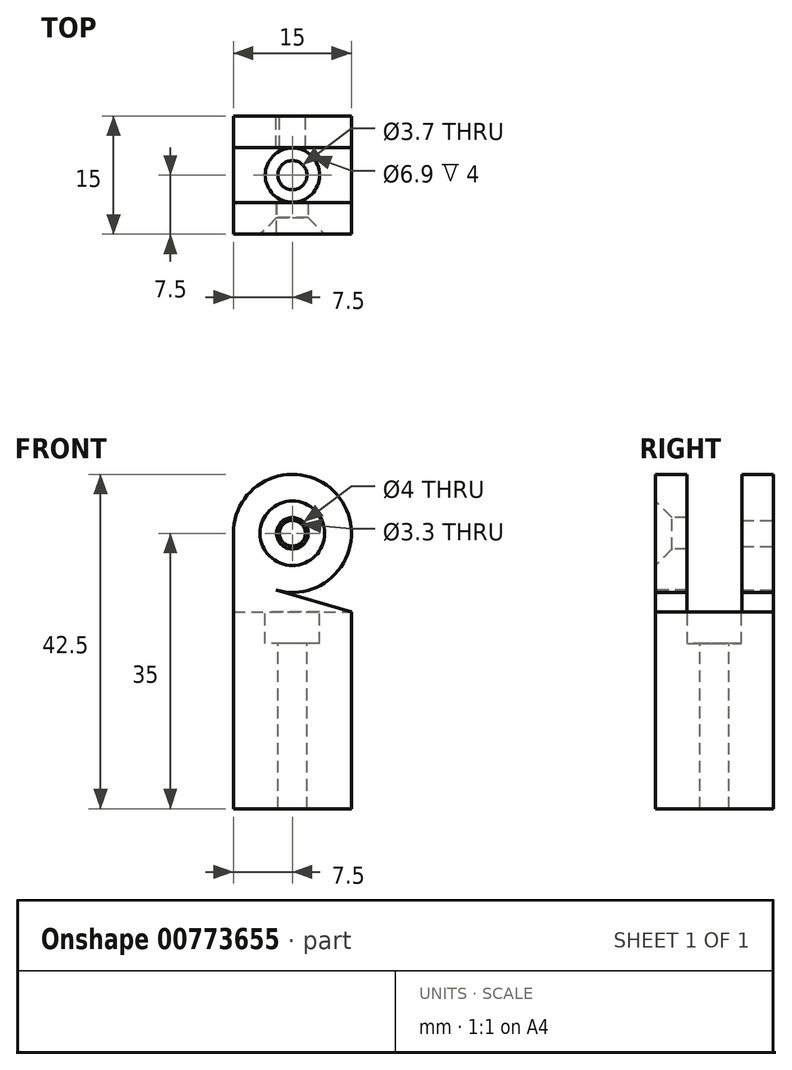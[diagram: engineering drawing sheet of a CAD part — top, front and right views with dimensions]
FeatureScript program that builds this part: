
annotation { "Feature Type Name" : "Feature", "Feature Type Description" : "" }
export const myFeature = defineFeature(function(context is Context, id is Id, definition is map)
    precondition{}
    {
        {
            var Q0;
            Q0=qCreatedBy(makeId("Top.planeOp"),FACE);
            var sketch = newSketch(context, id + "F0", { "sketchPlane" : qUnion([Q0])});
            skLineSegment(sketch, "E0", {"start": v(0, 0) * mm, "end": v(7.5, 0) * mm});
            skLineSegment(sketch, "E1", {"start": v(7.5, 0) * mm, "end": v(7.5, 7.5) * mm});
            skLineSegment(sketch, "E2", {"start": v(7.5, 7.5) * mm, "end": v(-7.5, 7.5) * mm});
            skLineSegment(sketch, "E3", {"start": v(-7.5, 7.5) * mm, "end": v(-7.5, -7.5) * mm});
            skLineSegment(sketch, "E4", {"start": v(-7.5, -7.5) * mm, "end": v(7.5, -7.5) * mm});
            skLineSegment(sketch, "E5", {"start": v(7.5, -7.5) * mm, "end": v(7.5, 0) * mm});
            skSolve(sketch);
        }
        {
            var Q0;
            Q0=makeQuery(id+"F0.imprint","IMPRINT",FACE,{"disambiguationData":[TD([[makeQuery(id+"F0.imprint","IMPRINT",EDGE,{"derivedFrom":sQuery(id+"F0.wireOp",EDGE,"E1")}),1.0]])]});
            extrude(context, id + "F1", {"entities" : qUnion([Q0]), "depth" : 25 * mm, "offsetDistance" : 25 * mm});
        }
        {
            var Q0;
            Q0=makeQuery(id+"F1.opExtrude","CAP_FACE",FACE,{"disambiguationData":[OSD([sQuery(id+"F0.wireOp",EDGE,"E1"),sQuery(id+"F0.wireOp",EDGE,"E2"),sQuery(id+"F0.wireOp",EDGE,"E3"),sQuery(id+"F0.wireOp",EDGE,"E4"),sQuery(id+"F0.wireOp",EDGE,"E5")])],"isStart":false});
            var sketch = newSketch(context, id + "F2", { "sketchPlane" : qUnion([Q0])});
            skPoint(sketch, "E6", {"position": v(0, 0) * mm});
            skSolve(sketch);
        }
        {
            var Q0;
            Q0=sQuery(id+"F2.wireOp",VERTEX,"E6");
            var Q1;
            Q1=makeQuery(id+"F1.opExtrude","SWEPT_BODY",BODY,{"disambiguationData":[OSD([sQuery(id+"F0.wireOp",EDGE,"E1"),sQuery(id+"F0.wireOp",EDGE,"E2"),sQuery(id+"F0.wireOp",EDGE,"E3"),sQuery(id+"F0.wireOp",EDGE,"E4"),sQuery(id+"F0.wireOp",EDGE,"E5")])]});
            hole(context, id + "F3", {"style" : HoleStyle.C_BORE, "endStyle" : HoleEndStyle.THROUGH, "holeDiameter" : 3.7 * mm, "cBoreDiameter" : 6.9 * mm, "cBoreDepth" : 4 * mm, "majorDiameter" : 5 * mm, "isTappedThrough" : true, "tappedDepth" : 12 * mm, "tapClearance" : 3, "locations" : qUnion([Q0]), "scope" : qUnion([Q1])});
        }
        {
            var Q0;
            Q0=makeQuery(id+"F1.opExtrude","SWEPT_FACE",FACE,{"disambiguationData":[OSD([sQuery(id+"F0.wireOp",EDGE,"E2")])]});
            var sketch = newSketch(context, id + "F4", { "sketchPlane" : qUnion([Q0])});
            skLineSegment(sketch, "E7", {"start": v(7.5, 25) * mm, "end": v(7.5, 35) * mm});
            skLineSegment(sketch, "E8", {"start": v(7.5, 35) * mm, "end": v(0, 35) * mm});
            skCircle(sketch, "E9", {"center": v(0, 35) * mm, "radius": 7.5 * mm});
            skLineSegment(sketch, "E10", {"start": v(-7.5, 25) * mm, "end": v(2.1, 27.8) * mm});
            skSolve(sketch);
        }
        {
            var Q0;
            {var subQ0=sQuery(id+"F4.wireOp",EDGE,"E7");Q0=makeQuery(id+"F4.imprint","IMPRINT",FACE,{"disambiguationData":[TD([[makeQuery(id+"F4.imprint","IMPRINT",EDGE,{"derivedFrom":subQ0}),1.0]])]});}
            var Q1;
            {var subQ0=sQuery(id+"F4.wireOp",EDGE,"E9");var subQ1=makeQuery(id+"F4.imprint","INTERSECT",VERTEX,{"derivedFrom":[sQuery(id+"F4.wireOp",EDGE,"E7"),subQ0]});Q1=makeQuery(id+"F4.imprint","IMPRINT",FACE,{"disambiguationData":[TD([[makeQuery(id+"F4.imprint","IMPRINT",EDGE,{"disambiguationData":[TD([[subQ1,-1.0]])],"derivedFrom":subQ0}),1.0]])]});}
            extrude(context, id + "F5", {"entities" : qUnion([Q0, Q1]), "operationType" : NewBodyOperationType.ADD, "oppositeDirection" : true, "depth" : 4 * mm, "offsetDistance" : 25 * mm});
        }
        {
            var Q0;
            Q0=makeQuery(id+"F1.opExtrude","SWEPT_FACE",FACE,{"disambiguationData":[OSD([sQuery(id+"F0.wireOp",EDGE,"E4")])]});
            var sketch = newSketch(context, id + "F6", { "sketchPlane" : qUnion([Q0])});
            skLineSegment(sketch, "E11", {"start": v(-7.5, 25) * mm, "end": v(-7.5, 35) * mm});
            skLineSegment(sketch, "E12", {"start": v(-7.5, 35) * mm, "end": v(0, 35) * mm});
            skCircle(sketch, "E13", {"center": v(0, 35) * mm, "radius": 7.5 * mm});
            skLineSegment(sketch, "E14", {"start": v(7.5, 25) * mm, "end": v(-2.1, 27.8) * mm});
            skSolve(sketch);
        }
        {
            var Q0;
            {var subQ0=sQuery(id+"F6.wireOp",EDGE,"E13");var subQ1=makeQuery(id+"F6.imprint","INTERSECT",VERTEX,{"derivedFrom":[sQuery(id+"F6.wireOp",EDGE,"E11"),subQ0]});Q0=makeQuery(id+"F6.imprint","IMPRINT",FACE,{"disambiguationData":[TD([[makeQuery(id+"F6.imprint","IMPRINT",EDGE,{"disambiguationData":[TD([[subQ1,-1.0]])],"derivedFrom":subQ0}),1.0]])]});}
            var Q1;
            {var subQ0=sQuery(id+"F6.wireOp",EDGE,"E11");Q1=makeQuery(id+"F6.imprint","IMPRINT",FACE,{"disambiguationData":[TD([[makeQuery(id+"F6.imprint","IMPRINT",EDGE,{"derivedFrom":subQ0}),-1.0]])]});}
            extrude(context, id + "F7", {"entities" : qUnion([Q0, Q1]), "operationType" : NewBodyOperationType.ADD, "oppositeDirection" : true, "depth" : 4 * mm, "offsetDistance" : 25 * mm});
        }
        {
            var Q0;
            {var subQ0=sQuery(id+"F0.wireOp",EDGE,"E4");Q0=makeQuery(id+"F7.boolean.opBoolean","MERGE",FACE,{"derivedFrom":[makeQuery(id+"F1.opExtrude","SWEPT_FACE",FACE,{"disambiguationData":[OSD([subQ0])]}),makeQuery(id+"F7.opExtrude","CAP_FACE",FACE,{"disambiguationData":[OSD([subQ0,sQuery(id+"F6.wireOp",EDGE,"E11"),sQuery(id+"F6.wireOp",EDGE,"E13"),sQuery(id+"F6.wireOp",EDGE,"E14")])],"isStart":true})]});}
            var sketch = newSketch(context, id + "F8", { "sketchPlane" : qUnion([Q0])});
            skLineSegment(sketch, "E15", {"start": v(-7.5, 35) * mm, "end": v(0, 35) * mm});
            skPoint(sketch, "E16", {"position": v(0, 35) * mm});
            skSolve(sketch);
        }
        {
            var Q0;
            Q0=sQuery(id+"F8.wireOp",VERTEX,"E16");
            var Q1;
            Q1=makeQuery(id+"F1.opExtrude","SWEPT_BODY",BODY,{"disambiguationData":[OSD([sQuery(id+"F0.wireOp",EDGE,"E1"),sQuery(id+"F0.wireOp",EDGE,"E2"),sQuery(id+"F0.wireOp",EDGE,"E3"),sQuery(id+"F0.wireOp",EDGE,"E4"),sQuery(id+"F0.wireOp",EDGE,"E5")])]});
            hole(context, id + "F9", {"style" : HoleStyle.C_SINK, "endStyle" : HoleEndStyle.BLIND, "holeDiameter" : 4 * mm, "cSinkDiameter" : 8.2 * mm, "cSinkAngle" : 90 * degree, "majorDiameter" : 5 * mm, "holeDepth" : 4 * mm, "isTappedThrough" : true, "tappedDepth" : 12 * mm, "tapClearance" : 3, "locations" : qUnion([Q0]), "scope" : qUnion([Q1])});
        }
        {
            var Q0;
            {var subQ0=sQuery(id+"F0.wireOp",EDGE,"E2");Q0=makeQuery(id+"F5.boolean.opBoolean","MERGE",FACE,{"derivedFrom":[makeQuery(id+"F1.opExtrude","SWEPT_FACE",FACE,{"disambiguationData":[OSD([subQ0])]}),makeQuery(id+"F5.opExtrude","CAP_FACE",FACE,{"disambiguationData":[OSD([subQ0,sQuery(id+"F4.wireOp",EDGE,"E7"),sQuery(id+"F4.wireOp",EDGE,"E9"),sQuery(id+"F4.wireOp",EDGE,"E10")])],"isStart":true})]});}
            var sketch = newSketch(context, id + "F10", { "sketchPlane" : qUnion([Q0])});
            skLineSegment(sketch, "E17", {"start": v(7.5, 35) * mm, "end": v(0, 35) * mm});
            skPoint(sketch, "E18", {"position": v(0, 35) * mm});
            skSolve(sketch);
        }
        {
            var Q0;
            Q0=sQuery(id+"F10.wireOp",VERTEX,"E18");
            var Q1;
            Q1=makeQuery(id+"F1.opExtrude","SWEPT_BODY",BODY,{"disambiguationData":[OSD([sQuery(id+"F0.wireOp",EDGE,"E1"),sQuery(id+"F0.wireOp",EDGE,"E2"),sQuery(id+"F0.wireOp",EDGE,"E3"),sQuery(id+"F0.wireOp",EDGE,"E4"),sQuery(id+"F0.wireOp",EDGE,"E5")])]});
            hole(context, id + "F11", {"style" : HoleStyle.SIMPLE, "endStyle" : HoleEndStyle.BLIND, "holeDiameter" : 3.3 * mm, "majorDiameter" : 5 * mm, "holeDepth" : 4 * mm, "isTappedThrough" : true, "tappedDepth" : 12 * mm, "tapClearance" : 3, "locations" : qUnion([Q0]), "scope" : qUnion([Q1])});
        }
    });
